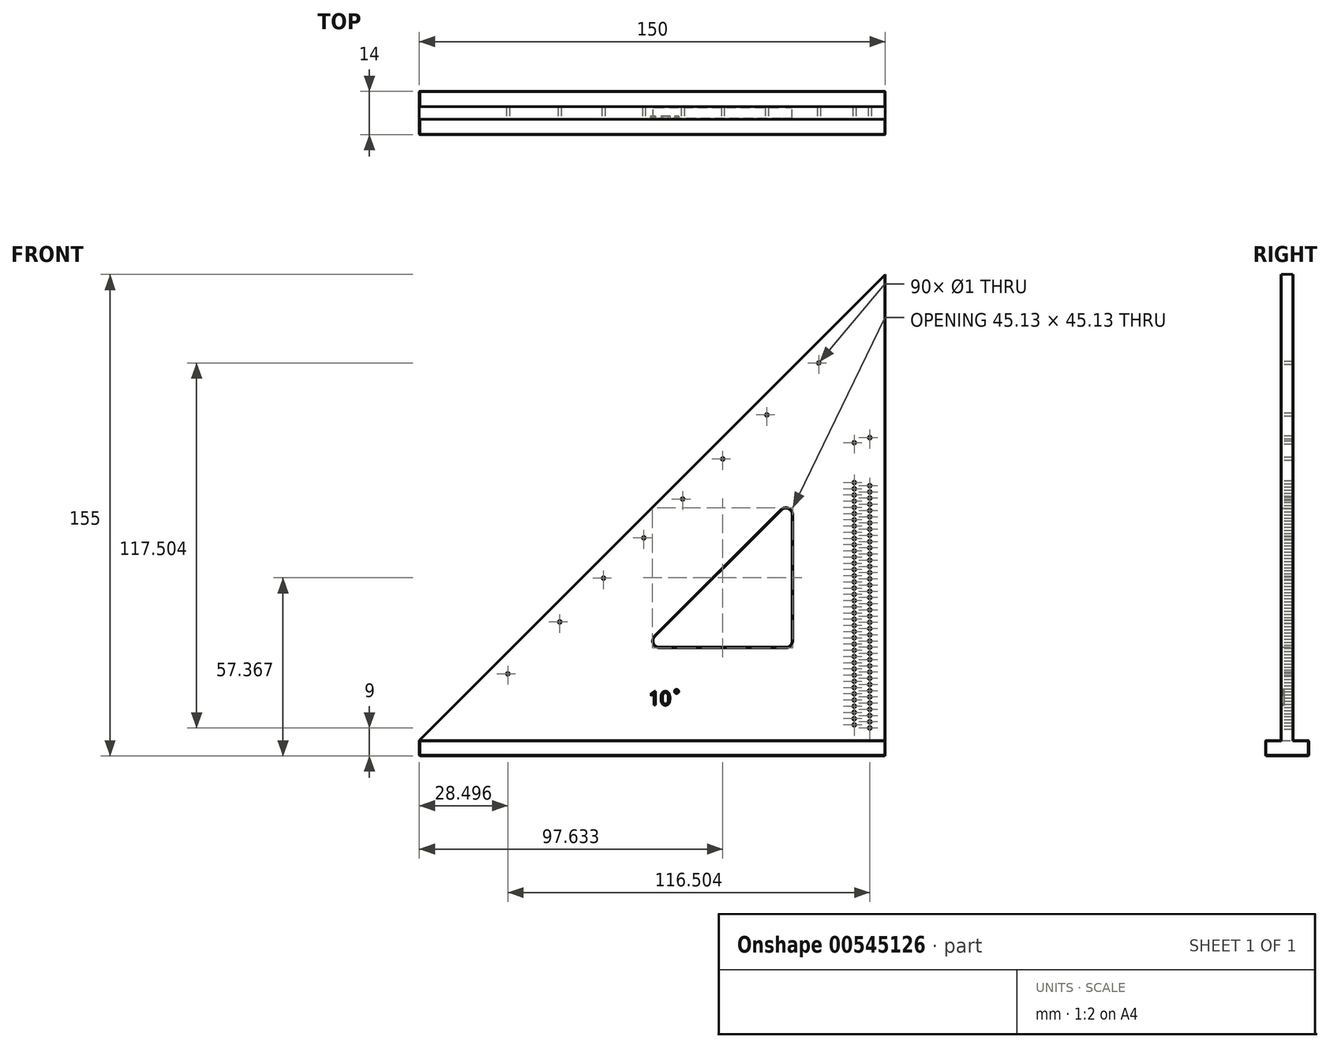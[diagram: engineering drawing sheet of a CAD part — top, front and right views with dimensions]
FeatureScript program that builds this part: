
annotation { "Feature Type Name" : "Feature", "Feature Type Description" : "" }
export const myFeature = defineFeature(function(context is Context, id is Id, definition is map)
    precondition{}
    {
        {
            var Q0;
            Q0=qCreatedBy(makeId("Front.planeOp"),FACE);
            var sketch = newSketch(context, id + "F0", { "sketchPlane" : qUnion([Q0])});
            skLineSegment(sketch, "E0", {"start": v(0, 0) * mm, "end": v(-150, 0) * mm});
            skLineSegment(sketch, "E1", {"start": v(-150, 0) * mm, "end": v(0, 150) * mm});
            skLineSegment(sketch, "E2", {"start": v(0, 150) * mm, "end": v(0, 0) * mm});
            skLineSegment(sketch, "E3", {"start": v(-74.16, 33.41) * mm, "end": v(-33.41, 74.16) * mm});
            skLineSegment(sketch, "E4", {"start": v(-30, 72.75) * mm, "end": v(-30, 32) * mm});
            skLineSegment(sketch, "E5", {"start": v(-32, 30) * mm, "end": v(-72.75, 30) * mm});
            skPoint(sketch, "E6.visualSharp", {"position": v(-30, 77.57) * mm});
            skArc(sketch, "E6.filletArc", {"start": v(-30, 72.75) * mm, "mid": v(-31.23, 74.6) * mm, "end": v(-33.41, 74.16) * mm});
            skPoint(sketch, "E7.visualSharp", {"position": v(-30, 30) * mm});
            skArc(sketch, "E7.filletArc", {"start": v(-32, 30) * mm, "mid": v(-30.59, 30.59) * mm, "end": v(-30, 32) * mm});
            skPoint(sketch, "E8.visualSharp", {"position": v(-77.57, 30) * mm});
            skArc(sketch, "E8.filletArc", {"start": v(-74.16, 33.41) * mm, "mid": v(-74.6, 31.23) * mm, "end": v(-72.75, 30) * mm});
            skSolve(sketch);
        }
        {
            var Q0;
            Q0=makeQuery(id+"F0.imprint","IMPRINT",FACE,{"disambiguationData":[TD([[makeQuery(id+"F0.imprint","IMPRINT",EDGE,{"derivedFrom":sQuery(id+"F0.wireOp",EDGE,"E0")}),-1.0]])]});
            extrude(context, id + "F1", {"entities" : qUnion([Q0]), "endBound" : BoundingType.SYMMETRIC, "depth" : 4 * mm, "offsetDistance" : 25 * mm});
        }
        {
            var Q0;
            Q0=qCreatedBy(makeId("Top.planeOp"),FACE);
            var sketch = newSketch(context, id + "F2", { "sketchPlane" : qUnion([Q0])});
            skLineSegment(sketch, "E9.bottom", {"start": v(-150, 7) * mm, "end": v(0, 7) * mm});
            skLineSegment(sketch, "E9.top", {"start": v(-150, -7) * mm, "end": v(0, -7) * mm});
            skLineSegment(sketch, "E9.left", {"start": v(-150, 7) * mm, "end": v(-150, -7) * mm});
            skLineSegment(sketch, "E9.right", {"start": v(0, 7) * mm, "end": v(0, -7) * mm});
            skSolve(sketch);
        }
        {
            var Q0;
            Q0=makeQuery(id+"F2.imprint","IMPRINT",FACE,{"disambiguationData":[TD([[makeQuery(id+"F2.imprint","IMPRINT",EDGE,{"derivedFrom":sQuery(id+"F2.wireOp",EDGE,"E9.bottom")}),-1.0]])]});
            extrude(context, id + "F3", {"entities" : qUnion([Q0]), "operationType" : NewBodyOperationType.ADD, "oppositeDirection" : true, "depth" : 5 * mm, "offsetDistance" : 25 * mm});
        }
        {
            var Q0;
            Q0=makeQuery(id+"F1.opExtrude","CAP_FACE",FACE,{"disambiguationData":[OSD([sQuery(id+"F0.wireOp",EDGE,"E0"),sQuery(id+"F0.wireOp",EDGE,"E1"),sQuery(id+"F0.wireOp",EDGE,"E2"),sQuery(id+"F0.wireOp",EDGE,"E3"),sQuery(id+"F0.wireOp",EDGE,"E4"),sQuery(id+"F0.wireOp",EDGE,"E5")])],"isStart":false});
            var sketch = newSketch(context, id + "F4", { "sketchPlane" : qUnion([Q0])});
            skLineSegment(sketch, "E10", {"start": v(-5, 97.46) * mm, "end": v(-5, 0) * mm, "construction": true});
            skLineSegment(sketch, "E11", {"start": v(-10, 95.84) * mm, "end": v(-10, 0) * mm, "construction": true});
            skPoint(sketch, "E12", {"position": v(-5, 4) * mm});
            skPoint(sketch, "E13", {"position": v(-10, 5) * mm});
            skPoint(sketch, "E14.0.1.0", {"position": v(-5, 6) * mm});
            skPoint(sketch, "E14.0.1.1", {"position": v(-10, 7) * mm});
            skPoint(sketch, "E14.0.2.0", {"position": v(-5, 8) * mm});
            skPoint(sketch, "E14.0.2.1", {"position": v(-10, 9) * mm});
            skPoint(sketch, "E14.0.3.0", {"position": v(-5, 10) * mm});
            skPoint(sketch, "E14.0.3.1", {"position": v(-10, 11) * mm});
            skPoint(sketch, "E14.0.4.0", {"position": v(-5, 12) * mm});
            skPoint(sketch, "E14.0.4.1", {"position": v(-10, 13) * mm});
            skPoint(sketch, "E14.0.5.0", {"position": v(-5, 14) * mm});
            skPoint(sketch, "E14.0.5.1", {"position": v(-10, 15) * mm});
            skPoint(sketch, "E14.0.6.0", {"position": v(-5, 16) * mm});
            skPoint(sketch, "E14.0.6.1", {"position": v(-10, 17) * mm});
            skPoint(sketch, "E14.0.7.0", {"position": v(-5, 18) * mm});
            skPoint(sketch, "E14.0.7.1", {"position": v(-10, 19) * mm});
            skPoint(sketch, "E14.0.8.0", {"position": v(-5, 20) * mm});
            skPoint(sketch, "E14.0.8.1", {"position": v(-10, 21) * mm});
            skPoint(sketch, "E14.0.9.0", {"position": v(-5, 22) * mm});
            skPoint(sketch, "E14.0.9.1", {"position": v(-10, 23) * mm});
            skPoint(sketch, "E14.0.10.0", {"position": v(-5, 24) * mm});
            skPoint(sketch, "E14.0.10.1", {"position": v(-10, 25) * mm});
            skPoint(sketch, "E14.0.11.0", {"position": v(-5, 26) * mm});
            skPoint(sketch, "E14.0.11.1", {"position": v(-10, 27) * mm});
            skPoint(sketch, "E14.0.12.0", {"position": v(-5, 28) * mm});
            skPoint(sketch, "E14.0.12.1", {"position": v(-10, 29) * mm});
            skPoint(sketch, "E14.0.13.0", {"position": v(-5, 30) * mm});
            skPoint(sketch, "E14.0.13.1", {"position": v(-10, 31) * mm});
            skPoint(sketch, "E14.0.14.0", {"position": v(-5, 32) * mm});
            skPoint(sketch, "E14.0.14.1", {"position": v(-10, 33) * mm});
            skPoint(sketch, "E14.0.15.0", {"position": v(-5, 34) * mm});
            skPoint(sketch, "E14.0.15.1", {"position": v(-10, 35) * mm});
            skPoint(sketch, "E14.0.16.0", {"position": v(-5, 36) * mm});
            skPoint(sketch, "E14.0.16.1", {"position": v(-10, 37) * mm});
            skPoint(sketch, "E14.0.17.0", {"position": v(-5, 38) * mm});
            skPoint(sketch, "E14.0.17.1", {"position": v(-10, 39) * mm});
            skPoint(sketch, "E14.0.18.0", {"position": v(-5, 40) * mm});
            skPoint(sketch, "E14.0.18.1", {"position": v(-10, 41) * mm});
            skPoint(sketch, "E14.0.19.0", {"position": v(-5, 42) * mm});
            skPoint(sketch, "E14.0.19.1", {"position": v(-10, 43) * mm});
            skPoint(sketch, "E14.0.20.0", {"position": v(-5, 44) * mm});
            skPoint(sketch, "E14.0.20.1", {"position": v(-10, 45) * mm});
            skPoint(sketch, "E14.0.21.0", {"position": v(-5, 46) * mm});
            skPoint(sketch, "E14.0.21.1", {"position": v(-10, 47) * mm});
            skPoint(sketch, "E14.0.22.0", {"position": v(-5, 48) * mm});
            skPoint(sketch, "E14.0.22.1", {"position": v(-10, 49) * mm});
            skPoint(sketch, "E14.0.23.0", {"position": v(-5, 50) * mm});
            skPoint(sketch, "E14.0.23.1", {"position": v(-10, 51) * mm});
            skPoint(sketch, "E14.0.24.0", {"position": v(-5, 52) * mm});
            skPoint(sketch, "E14.0.24.1", {"position": v(-10, 53) * mm});
            skPoint(sketch, "E14.0.25.0", {"position": v(-5, 54) * mm});
            skPoint(sketch, "E14.0.25.1", {"position": v(-10, 55) * mm});
            skPoint(sketch, "E14.0.26.0", {"position": v(-5, 56) * mm});
            skPoint(sketch, "E14.0.26.1", {"position": v(-10, 57) * mm});
            skPoint(sketch, "E14.0.27.0", {"position": v(-5, 58) * mm});
            skPoint(sketch, "E14.0.27.1", {"position": v(-10, 59) * mm});
            skPoint(sketch, "E14.0.28.0", {"position": v(-5, 60) * mm});
            skPoint(sketch, "E14.0.28.1", {"position": v(-10, 61) * mm});
            skPoint(sketch, "E14.0.29.0", {"position": v(-5, 62) * mm});
            skPoint(sketch, "E14.0.29.1", {"position": v(-10, 63) * mm});
            skPoint(sketch, "E14.0.30.0", {"position": v(-5, 64) * mm});
            skPoint(sketch, "E14.0.30.1", {"position": v(-10, 65) * mm});
            skPoint(sketch, "E14.0.31.0", {"position": v(-5, 66) * mm});
            skPoint(sketch, "E14.0.31.1", {"position": v(-10, 67) * mm});
            skPoint(sketch, "E14.0.32.0", {"position": v(-5, 68) * mm});
            skPoint(sketch, "E14.0.32.1", {"position": v(-10, 69) * mm});
            skPoint(sketch, "E14.0.33.0", {"position": v(-5, 70) * mm});
            skPoint(sketch, "E14.0.33.1", {"position": v(-10, 71) * mm});
            skPoint(sketch, "E14.0.34.0", {"position": v(-5, 72) * mm});
            skPoint(sketch, "E14.0.34.1", {"position": v(-10, 73) * mm});
            skPoint(sketch, "E14.0.35.0", {"position": v(-5, 74) * mm});
            skPoint(sketch, "E14.0.35.1", {"position": v(-10, 75) * mm});
            skPoint(sketch, "E14.0.36.0", {"position": v(-5, 76) * mm});
            skPoint(sketch, "E14.0.36.1", {"position": v(-10, 77) * mm});
            skPoint(sketch, "E14.0.37.0", {"position": v(-5, 78) * mm});
            skPoint(sketch, "E14.0.37.1", {"position": v(-10, 79) * mm});
            skPoint(sketch, "E14.0.38.0", {"position": v(-5, 80) * mm});
            skPoint(sketch, "E14.0.38.1", {"position": v(-10, 81) * mm});
            skPoint(sketch, "E14.0.39.0", {"position": v(-5, 82) * mm});
            skPoint(sketch, "E14.0.39.1", {"position": v(-10, 83) * mm});
            skLineSegment(sketch, "E14.direction1", {"start": v(-10, 5) * mm, "end": v(15, 5) * mm, "construction": true});
            skLineSegment(sketch, "E14.direction2", {"start": v(-10, 5) * mm, "end": v(-10, 7) * mm, "construction": true});
            skSolve(sketch);
        }
        {
            var Q0;
            Q0=sQuery(id+"F4.wireOp",VERTEX,"E14.0.29.0");
            var Q1;
            Q1=sQuery(id+"F4.wireOp",VERTEX,"E14.0.21.0");
            var Q2;
            Q2=sQuery(id+"F4.wireOp",VERTEX,"E14.0.13.0");
            var Q3;
            Q3=sQuery(id+"F4.wireOp",VERTEX,"E14.0.5.0");
            var Q4;
            Q4=sQuery(id+"F4.wireOp",VERTEX,"E14.0.32.1");
            var Q5;
            Q5=sQuery(id+"F4.wireOp",VERTEX,"E14.0.24.1");
            var Q6;
            Q6=sQuery(id+"F4.wireOp",VERTEX,"E14.0.39.1");
            var Q7;
            Q7=sQuery(id+"F4.wireOp",VERTEX,"E14.0.34.0");
            var Q8;
            Q8=sQuery(id+"F4.wireOp",VERTEX,"E11.start");
            var Q9;
            Q9=sQuery(id+"F4.wireOp",VERTEX,"E14.0.30.1");
            var Q10;
            Q10=sQuery(id+"F4.wireOp",VERTEX,"E14.0.22.1");
            var Q11;
            Q11=sQuery(id+"F4.wireOp",VERTEX,"E14.0.6.1");
            var Q12;
            Q12=sQuery(id+"F4.wireOp",VERTEX,"E14.0.31.0");
            var Q13;
            Q13=sQuery(id+"F4.wireOp",VERTEX,"E14.0.23.0");
            var Q14;
            Q14=sQuery(id+"F4.wireOp",VERTEX,"E14.0.14.1");
            var Q15;
            Q15=sQuery(id+"F4.wireOp",VERTEX,"E14.0.38.1");
            var Q16;
            Q16=sQuery(id+"F4.wireOp",VERTEX,"E14.0.19.1");
            var Q17;
            Q17=sQuery(id+"F4.wireOp",VERTEX,"E12");
            var Q18;
            Q18=sQuery(id+"F4.wireOp",VERTEX,"E10.start");
            var Q19;
            Q19=sQuery(id+"F4.wireOp",VERTEX,"E13");
            var Q20;
            Q20=sQuery(id+"F4.wireOp",VERTEX,"E14.0.28.1");
            var Q21;
            Q21=sQuery(id+"F4.wireOp",VERTEX,"E14.0.20.1");
            var Q22;
            Q22=sQuery(id+"F4.wireOp",VERTEX,"E14.0.12.1");
            var Q23;
            Q23=sQuery(id+"F4.wireOp",VERTEX,"E14.0.4.1");
            var Q24;
            Q24=sQuery(id+"F4.wireOp",VERTEX,"E14.0.36.1");
            var Q25;
            Q25=sQuery(id+"F4.wireOp",VERTEX,"E14.0.10.0");
            var Q26;
            Q26=sQuery(id+"F4.wireOp",VERTEX,"E14.0.18.0");
            var Q27;
            Q27=sQuery(id+"F4.wireOp",VERTEX,"E14.0.26.0");
            var Q28;
            Q28=sQuery(id+"F4.wireOp",VERTEX,"E14.0.3.1");
            var Q29;
            Q29=sQuery(id+"F4.wireOp",VERTEX,"E14.0.1.0");
            var Q30;
            Q30=sQuery(id+"F4.wireOp",VERTEX,"E14.0.16.0");
            var Q31;
            Q31=sQuery(id+"F4.wireOp",VERTEX,"E14.0.8.0");
            var Q32;
            Q32=sQuery(id+"F4.wireOp",VERTEX,"E14.0.15.0");
            var Q33;
            Q33=sQuery(id+"F4.wireOp",VERTEX,"E14.0.7.0");
            var Q34;
            Q34=sQuery(id+"F4.wireOp",VERTEX,"E14.0.27.1");
            var Q35;
            Q35=sQuery(id+"F4.wireOp",VERTEX,"E14.0.1.1");
            var Q36;
            Q36=sQuery(id+"F4.wireOp",VERTEX,"E14.0.11.1");
            var Q37;
            Q37=sQuery(id+"F4.wireOp",VERTEX,"E14.0.2.0");
            var Q38;
            Q38=sQuery(id+"F4.wireOp",VERTEX,"E14.0.16.1");
            var Q39;
            Q39=sQuery(id+"F4.wireOp",VERTEX,"E14.0.37.0");
            var Q40;
            Q40=sQuery(id+"F4.wireOp",VERTEX,"E14.0.8.1");
            var Q41;
            Q41=sQuery(id+"F4.wireOp",VERTEX,"E14.0.35.1");
            var Q42;
            Q42=sQuery(id+"F4.wireOp",VERTEX,"E14.0.39.0");
            var Q43;
            Q43=sQuery(id+"F4.wireOp",VERTEX,"E14.0.22.0");
            var Q44;
            Q44=sQuery(id+"F4.wireOp",VERTEX,"E14.0.26.1");
            var Q45;
            Q45=sQuery(id+"F4.wireOp",VERTEX,"E14.0.30.0");
            var Q46;
            Q46=sQuery(id+"F4.wireOp",VERTEX,"E14.0.34.1");
            var Q47;
            Q47=sQuery(id+"F4.wireOp",VERTEX,"E14.0.15.1");
            var Q48;
            Q48=sQuery(id+"F4.wireOp",VERTEX,"E14.0.7.1");
            var Q49;
            Q49=sQuery(id+"F4.wireOp",VERTEX,"E14.0.31.1");
            var Q50;
            Q50=sQuery(id+"F4.wireOp",VERTEX,"E14.0.23.1");
            var Q51;
            Q51=sQuery(id+"F4.wireOp",VERTEX,"E14.0.29.1");
            var Q52;
            Q52=sQuery(id+"F4.wireOp",VERTEX,"E14.0.18.1");
            var Q53;
            Q53=sQuery(id+"F4.wireOp",VERTEX,"E14.0.9.1");
            var Q54;
            Q54=sQuery(id+"F4.wireOp",VERTEX,"E14.0.33.1");
            var Q55;
            Q55=sQuery(id+"F4.wireOp",VERTEX,"E14.0.25.1");
            var Q56;
            Q56=sQuery(id+"F4.wireOp",VERTEX,"E14.0.27.0");
            var Q57;
            Q57=sQuery(id+"F4.wireOp",VERTEX,"E14.0.2.1");
            var Q58;
            Q58=sQuery(id+"F4.wireOp",VERTEX,"E14.0.20.0");
            var Q59;
            Q59=sQuery(id+"F4.wireOp",VERTEX,"E14.0.28.0");
            var Q60;
            Q60=sQuery(id+"F4.wireOp",VERTEX,"E14.0.4.0");
            var Q61;
            Q61=sQuery(id+"F4.wireOp",VERTEX,"E14.0.12.0");
            var Q62;
            Q62=sQuery(id+"F4.wireOp",VERTEX,"E14.0.36.0");
            var Q63;
            Q63=sQuery(id+"F4.wireOp",VERTEX,"E14.0.14.0");
            var Q64;
            Q64=sQuery(id+"F4.wireOp",VERTEX,"E14.0.17.1");
            var Q65;
            Q65=sQuery(id+"F4.wireOp",VERTEX,"E14.0.21.1");
            var Q66;
            Q66=sQuery(id+"F4.wireOp",VERTEX,"E14.0.19.0");
            var Q67;
            Q67=sQuery(id+"F4.wireOp",VERTEX,"E14.0.37.1");
            var Q68;
            Q68=sQuery(id+"F4.wireOp",VERTEX,"E14.0.10.1");
            var Q69;
            Q69=sQuery(id+"F4.wireOp",VERTEX,"E14.0.17.0");
            var Q70;
            Q70=sQuery(id+"F4.wireOp",VERTEX,"E14.0.11.0");
            var Q71;
            Q71=sQuery(id+"F4.wireOp",VERTEX,"E14.0.35.0");
            var Q72;
            Q72=sQuery(id+"F4.wireOp",VERTEX,"E14.0.32.0");
            var Q73;
            Q73=sQuery(id+"F4.wireOp",VERTEX,"E14.0.6.0");
            var Q74;
            Q74=sQuery(id+"F4.wireOp",VERTEX,"E14.0.24.0");
            var Q75;
            Q75=sQuery(id+"F4.wireOp",VERTEX,"E14.0.13.1");
            var Q76;
            Q76=sQuery(id+"F4.wireOp",VERTEX,"E14.0.3.0");
            var Q77;
            Q77=sQuery(id+"F4.wireOp",VERTEX,"E14.0.5.1");
            var Q78;
            Q78=sQuery(id+"F4.wireOp",VERTEX,"E14.0.38.0");
            var Q79;
            Q79=sQuery(id+"F4.wireOp",VERTEX,"E14.0.9.0");
            var Q80;
            Q80=sQuery(id+"F4.wireOp",VERTEX,"E14.0.33.0");
            var Q81;
            Q81=sQuery(id+"F4.wireOp",VERTEX,"E14.0.25.0");
            var Q82;
            Q82=makeQuery(id+"F1.opExtrude","SWEPT_BODY",BODY,{"disambiguationData":[OSD([sQuery(id+"F0.wireOp",EDGE,"E0"),sQuery(id+"F0.wireOp",EDGE,"E1"),sQuery(id+"F0.wireOp",EDGE,"E2"),sQuery(id+"F0.wireOp",EDGE,"E3"),sQuery(id+"F0.wireOp",EDGE,"E4"),sQuery(id+"F0.wireOp",EDGE,"E5")])]});
            hole(context, id + "F5", {"style" : HoleStyle.SIMPLE, "endStyle" : HoleEndStyle.BLIND, "holeDiameter" : 1 * mm, "holeDepth" : 10 * mm, "isTappedThrough" : true, "tappedDepth" : 12 * mm, "tapClearance" : 3, "locations" : qUnion([Q0, Q1, Q2, Q3, Q4, Q5, Q6, Q7, Q8, Q9, Q10, Q11, Q12, Q13, Q14, Q15, Q16, Q17, Q18, Q19, Q20, Q21, Q22, Q23, Q24, Q25, Q26, Q27, Q28, Q29, Q30, Q31, Q32, Q33, Q34, Q35, Q36, Q37, Q38, Q39, Q40, Q41, Q42, Q43, Q44, Q45, Q46, Q47, Q48, Q49, Q50, Q51, Q52, Q53, Q54, Q55, Q56, Q57, Q58, Q59, Q60, Q61, Q62, Q63, Q64, Q65, Q66, Q67, Q68, Q69, Q70, Q71, Q72, Q73, Q74, Q75, Q76, Q77, Q78, Q79, Q80, Q81]), "scope" : qUnion([Q82])});
        }
        {
            var Q0;
            Q0=makeQuery(id+"F1.opExtrude","CAP_EDGE",EDGE,{"disambiguationData":[OSD([sQuery(id+"F0.wireOp",EDGE,"E2")])],"isStart":true});
            var Q1;
            Q1=makeQuery(id+"F1.opExtrude","CAP_EDGE",EDGE,{"disambiguationData":[OSD([sQuery(id+"F0.wireOp",EDGE,"E2")])],"isStart":false});
            var Q2;
            {var subQ0=sQuery(id+"F2.wireOp",EDGE,"E9.right");var subQ1=sQuery(id+"F2.wireOp",EDGE,"E9.bottom");Q2=makeQuery(id+"F3.boolean.opBoolean","SPLIT",EDGE,{"disambiguationData":[TD([makeQuery(id+"F3.opExtrude","SWEPT_FACE",FACE,{"disambiguationData":[OSD([subQ1])]})])],"derivedFrom":makeQuery(id+"F3.opExtrude","CAP_EDGE",EDGE,{"disambiguationData":[OSD([subQ0])],"isStart":true})});}
            var Q3;
            Q3=makeQuery(id+"F3.opExtrude","SWEPT_EDGE",EDGE,{"disambiguationData":[OSD([sQuery(id+"F2.wireOp",EDGE,"E9.bottom"),sQuery(id+"F2.wireOp",EDGE,"E9.right")])]});
            var Q4;
            Q4=makeQuery(id+"F3.opExtrude","CAP_EDGE",EDGE,{"disambiguationData":[OSD([sQuery(id+"F2.wireOp",EDGE,"E9.bottom")])],"isStart":true});
            var Q5;
            Q5=makeQuery(id+"F3.opExtrude","CAP_EDGE",EDGE,{"disambiguationData":[OSD([sQuery(id+"F2.wireOp",EDGE,"E9.bottom")])],"isStart":false});
            var Q6;
            Q6=makeQuery(id+"F3.opExtrude","CAP_EDGE",EDGE,{"disambiguationData":[OSD([sQuery(id+"F2.wireOp",EDGE,"E9.right")])],"isStart":false});
            var Q7;
            Q7=makeQuery(id+"F3.opExtrude","SWEPT_EDGE",EDGE,{"disambiguationData":[OSD([sQuery(id+"F2.wireOp",EDGE,"E9.top"),sQuery(id+"F2.wireOp",EDGE,"E9.right")])]});
            var Q8;
            {var subQ0=sQuery(id+"F2.wireOp",EDGE,"E9.right");var subQ1=sQuery(id+"F2.wireOp",EDGE,"E9.top");Q8=makeQuery(id+"F3.boolean.opBoolean","SPLIT",EDGE,{"disambiguationData":[TD([makeQuery(id+"F3.opExtrude","SWEPT_FACE",FACE,{"disambiguationData":[OSD([subQ1])]})])],"derivedFrom":makeQuery(id+"F3.opExtrude","CAP_EDGE",EDGE,{"disambiguationData":[OSD([subQ0])],"isStart":true})});}
            var Q9;
            Q9=makeQuery(id+"F1.opExtrude","CAP_EDGE",EDGE,{"disambiguationData":[OSD([sQuery(id+"F0.wireOp",EDGE,"E5")])],"isStart":true});
            var Q10;
            Q10=makeQuery(id+"F3.opExtrude","CAP_EDGE",EDGE,{"disambiguationData":[OSD([sQuery(id+"F2.wireOp",EDGE,"E9.left")])],"isStart":false});
            var Q11;
            Q11=makeQuery(id+"F3.opExtrude","SWEPT_EDGE",EDGE,{"disambiguationData":[OSD([sQuery(id+"F2.wireOp",EDGE,"E9.top"),sQuery(id+"F2.wireOp",EDGE,"E9.left")])]});
            var Q12;
            {var subQ0=sQuery(id+"F2.wireOp",EDGE,"E9.left");var subQ1=sQuery(id+"F2.wireOp",EDGE,"E9.top");Q12=makeQuery(id+"F3.boolean.opBoolean","SPLIT",EDGE,{"disambiguationData":[TD([makeQuery(id+"F3.opExtrude","SWEPT_FACE",FACE,{"disambiguationData":[OSD([subQ1])]})])],"derivedFrom":makeQuery(id+"F3.opExtrude","CAP_EDGE",EDGE,{"disambiguationData":[OSD([subQ0])],"isStart":true})});}
            var Q13;
            {var subQ0=sQuery(id+"F2.wireOp",EDGE,"E9.left");var subQ1=sQuery(id+"F2.wireOp",EDGE,"E9.bottom");Q13=makeQuery(id+"F3.boolean.opBoolean","SPLIT",EDGE,{"disambiguationData":[TD([makeQuery(id+"F3.opExtrude","SWEPT_FACE",FACE,{"disambiguationData":[OSD([subQ1])]})])],"derivedFrom":makeQuery(id+"F3.opExtrude","CAP_EDGE",EDGE,{"disambiguationData":[OSD([subQ0])],"isStart":true})});}
            var Q14;
            Q14=makeQuery(id+"F3.opExtrude","SWEPT_EDGE",EDGE,{"disambiguationData":[OSD([sQuery(id+"F2.wireOp",EDGE,"E9.bottom"),sQuery(id+"F2.wireOp",EDGE,"E9.left")])]});
            var Q15;
            Q15=makeQuery(id+"F3.opExtrude","CAP_EDGE",EDGE,{"disambiguationData":[OSD([sQuery(id+"F2.wireOp",EDGE,"E9.top")])],"isStart":false});
            var Q16;
            Q16=makeQuery(id+"F3.opExtrude","CAP_EDGE",EDGE,{"disambiguationData":[OSD([sQuery(id+"F2.wireOp",EDGE,"E9.top")])],"isStart":true});
            var Q17;
            Q17=makeQuery(id+"F1.opExtrude","CAP_EDGE",EDGE,{"disambiguationData":[OSD([sQuery(id+"F0.wireOp",EDGE,"E4")])],"isStart":false});
            var Q18;
            Q18=makeQuery(id+"F1.opExtrude","CAP_EDGE",EDGE,{"disambiguationData":[OSD([sQuery(id+"F0.wireOp",EDGE,"E6.filletArc")])],"isStart":false});
            var Q19;
            Q19=makeQuery(id+"F1.opExtrude","CAP_EDGE",EDGE,{"disambiguationData":[OSD([sQuery(id+"F0.wireOp",EDGE,"E3")])],"isStart":false});
            var Q20;
            Q20=makeQuery(id+"F1.opExtrude","CAP_EDGE",EDGE,{"disambiguationData":[OSD([sQuery(id+"F0.wireOp",EDGE,"E8.filletArc")])],"isStart":false});
            var Q21;
            Q21=makeQuery(id+"F1.opExtrude","CAP_EDGE",EDGE,{"disambiguationData":[OSD([sQuery(id+"F0.wireOp",EDGE,"E5")])],"isStart":false});
            var Q22;
            Q22=makeQuery(id+"F1.opExtrude","CAP_EDGE",EDGE,{"disambiguationData":[OSD([sQuery(id+"F0.wireOp",EDGE,"E7.filletArc")])],"isStart":false});
            var Q23;
            Q23=makeQuery(id+"F1.opExtrude","CAP_EDGE",EDGE,{"disambiguationData":[OSD([sQuery(id+"F0.wireOp",EDGE,"E8.filletArc")])],"isStart":true});
            var Q24;
            Q24=makeQuery(id+"F1.opExtrude","CAP_EDGE",EDGE,{"disambiguationData":[OSD([sQuery(id+"F0.wireOp",EDGE,"E3")])],"isStart":true});
            var Q25;
            Q25=makeQuery(id+"F1.opExtrude","CAP_EDGE",EDGE,{"disambiguationData":[OSD([sQuery(id+"F0.wireOp",EDGE,"E6.filletArc")])],"isStart":true});
            var Q26;
            Q26=makeQuery(id+"F1.opExtrude","CAP_EDGE",EDGE,{"disambiguationData":[OSD([sQuery(id+"F0.wireOp",EDGE,"E4")])],"isStart":true});
            var Q27;
            Q27=makeQuery(id+"F1.opExtrude","CAP_EDGE",EDGE,{"disambiguationData":[OSD([sQuery(id+"F0.wireOp",EDGE,"E7.filletArc")])],"isStart":true});
            chamfer(context, id + "F6", {"entities" : qUnion([Q0, Q1, Q2, Q3, Q4, Q5, Q6, Q7, Q8, Q9, Q10, Q11, Q12, Q13, Q14, Q15, Q16, Q17, Q18, Q19, Q20, Q21, Q22, Q23, Q24, Q25, Q26, Q27]), "width" : 0.2 * mm, "tangentPropagation" : true});
        }
        {
            var Q0;
            Q0=makeQuery(id+"F1.opExtrude","CAP_FACE",FACE,{"disambiguationData":[OSD([sQuery(id+"F0.wireOp",EDGE,"E0"),sQuery(id+"F0.wireOp",EDGE,"E1"),sQuery(id+"F0.wireOp",EDGE,"E2"),sQuery(id+"F0.wireOp",EDGE,"E3"),sQuery(id+"F0.wireOp",EDGE,"E4"),sQuery(id+"F0.wireOp",EDGE,"E5"),sQuery(id+"F0.wireOp",EDGE,"E6.filletArc"),sQuery(id+"F0.wireOp",EDGE,"E7.filletArc"),sQuery(id+"F0.wireOp",EDGE,"E8.filletArc")])],"isStart":false});
            var sketch = newSketch(context, id + "F7", { "sketchPlane" : qUnion([Q0])});
            skLineSegment(sketch, "E15", {"start": v(0, 0) * mm, "end": v(-99.41, 36.18) * mm, "construction": true});
            skLineSegment(sketch, "E16", {"start": v(0, 0) * mm, "end": v(-79.68, 66.86) * mm, "construction": true});
            skLineSegment(sketch, "E17", {"start": v(0, 0) * mm, "end": v(-51, 88.33) * mm, "construction": true});
            skLineSegment(sketch, "E18", {"start": v(0, 0) * mm, "end": v(-34.37, 94.42) * mm, "construction": true});
            skLineSegment(sketch, "E19", {"start": v(0, 0) * mm, "end": v(-17.7, 100.36) * mm, "construction": true});
            skLineSegment(sketch, "E20", {"start": v(0, 0) * mm, "end": v(-63.79, 76.02) * mm, "construction": true});
            skLineSegment(sketch, "E21", {"start": v(-0.2, 0) * mm, "end": v(-91.15, 52.5) * mm, "construction": true});
            skLineSegment(sketch, "E22", {"start": v(0, 0) * mm, "end": v(-102.48, 18.07) * mm, "construction": true});
            skLineSegment(sketch, "E23", {"start": v(-121.5, 21.42) * mm, "end": v(-21.42, 121.5) * mm, "construction": true});
            skPoint(sketch, "E24", {"position": v(-121.5, 21.42) * mm});
            skPoint(sketch, "E25", {"position": v(-104.79, 38.14) * mm});
            skPoint(sketch, "E26", {"position": v(-90.69, 52.24) * mm});
            skPoint(sketch, "E27", {"position": v(-77.72, 65.21) * mm});
            skPoint(sketch, "E28", {"position": v(-65.21, 77.72) * mm});
            skPoint(sketch, "E29", {"position": v(-52.32, 90.61) * mm});
            skPoint(sketch, "E30", {"position": v(-38.14, 104.79) * mm});
            skPoint(sketch, "E31", {"position": v(-21.42, 121.5) * mm});
            skSolve(sketch);
        }
        {
            var Q0;
            Q0=sQuery(id+"F7.wireOp",VERTEX,"E24");
            var Q1;
            Q1=sQuery(id+"F7.wireOp",VERTEX,"E25");
            var Q2;
            Q2=sQuery(id+"F7.wireOp",VERTEX,"E28");
            var Q3;
            Q3=sQuery(id+"F7.wireOp",VERTEX,"E26");
            var Q4;
            Q4=sQuery(id+"F7.wireOp",VERTEX,"E27");
            var Q5;
            Q5=sQuery(id+"F7.wireOp",VERTEX,"E29");
            var Q6;
            Q6=sQuery(id+"F7.wireOp",VERTEX,"E31");
            var Q7;
            Q7=sQuery(id+"F7.wireOp",VERTEX,"E30");
            var Q8;
            Q8=makeQuery(id+"F1.opExtrude","SWEPT_BODY",BODY,{"disambiguationData":[OSD([sQuery(id+"F0.wireOp",EDGE,"E0"),sQuery(id+"F0.wireOp",EDGE,"E1"),sQuery(id+"F0.wireOp",EDGE,"E2"),sQuery(id+"F0.wireOp",EDGE,"E3"),sQuery(id+"F0.wireOp",EDGE,"E4"),sQuery(id+"F0.wireOp",EDGE,"E5"),sQuery(id+"F0.wireOp",EDGE,"E6.filletArc"),sQuery(id+"F0.wireOp",EDGE,"E7.filletArc"),sQuery(id+"F0.wireOp",EDGE,"E8.filletArc")])]});
            hole(context, id + "F8", {"style" : HoleStyle.SIMPLE, "endStyle" : HoleEndStyle.BLIND, "holeDiameter" : 1 * mm, "holeDepth" : 10 * mm, "isTappedThrough" : true, "tappedDepth" : 12 * mm, "tapClearance" : 3, "locations" : qUnion([Q0, Q1, Q2, Q3, Q4, Q5, Q6, Q7]), "scope" : qUnion([Q8])});
        }
        {
            var Q0;
            Q0=makeQuery(id+"F1.opExtrude","CAP_FACE",FACE,{"disambiguationData":[OSD([sQuery(id+"F0.wireOp",EDGE,"E0"),sQuery(id+"F0.wireOp",EDGE,"E1"),sQuery(id+"F0.wireOp",EDGE,"E2"),sQuery(id+"F0.wireOp",EDGE,"E3"),sQuery(id+"F0.wireOp",EDGE,"E4"),sQuery(id+"F0.wireOp",EDGE,"E5"),sQuery(id+"F0.wireOp",EDGE,"E6.filletArc"),sQuery(id+"F0.wireOp",EDGE,"E7.filletArc"),sQuery(id+"F0.wireOp",EDGE,"E8.filletArc")])],"isStart":false});
            var sketch = newSketch(context, id + "F9", { "sketchPlane" : qUnion([Q0])});
            skText(sketch, "E32", { "text": "10˚", "fontName": "NotoSans-Regular.ttf"});
            const initialGuessF9  = {"E32": [-0.07611, 0.01134, 1, 0, 0.00448]};
            skSetInitialGuess(sketch, initialGuessF9);
            skSolve(sketch);
        }
        {
            var Q0;
            Q0 = qSketchRegion(id + "F9", true);
            extrude(context, id + "F10", {"entities" : qUnion([Q0]), "operationType" : NewBodyOperationType.REMOVE, "oppositeDirection" : true, "depth" : 1 * mm, "offsetDistance" : 25 * mm});
        }
    });
